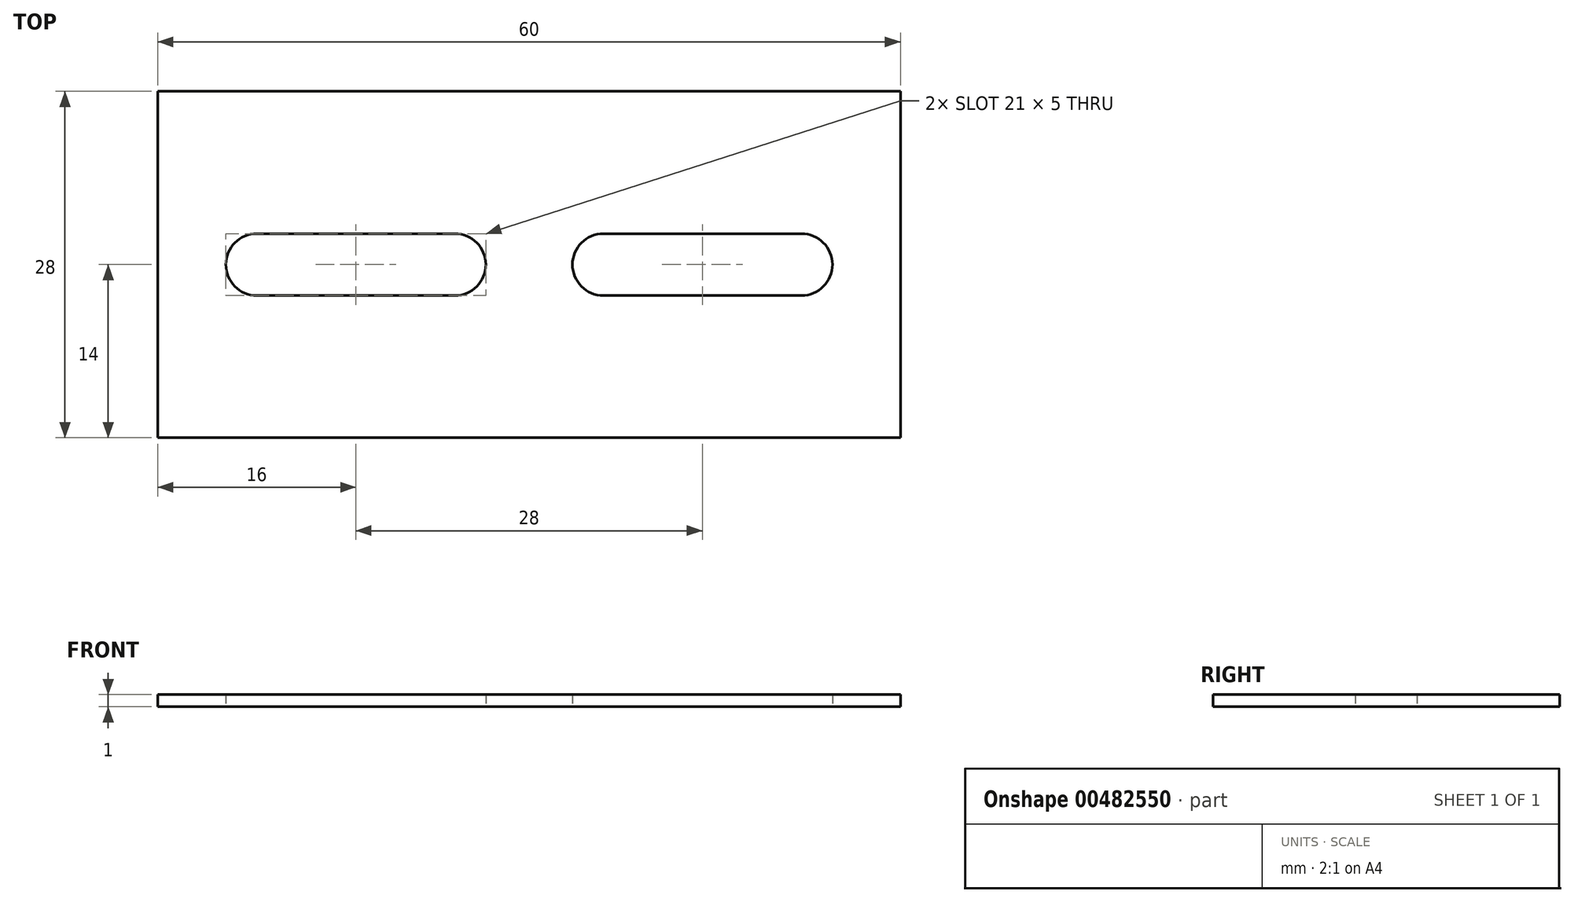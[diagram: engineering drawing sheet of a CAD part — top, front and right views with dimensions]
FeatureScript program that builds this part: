
annotation { "Feature Type Name" : "Feature", "Feature Type Description" : "" }
export const myFeature = defineFeature(function(context is Context, id is Id, definition is map)
    precondition{}
    {
        {
            var Q0;
            Q0=qCreatedBy(makeId("Top.planeOp"),FACE);
            var sketch = newSketch(context, id + "F0", { "sketchPlane" : qUnion([Q0])});
            skLineSegment(sketch, "E0.bottom", {"start": v(30, 14) * mm, "end": v(-30, 14) * mm});
            skLineSegment(sketch, "E0.top", {"start": v(30, -14) * mm, "end": v(-30, -14) * mm});
            skLineSegment(sketch, "E0.left", {"start": v(30, 14) * mm, "end": v(30, -14) * mm});
            skLineSegment(sketch, "E0.right", {"start": v(-30, 14) * mm, "end": v(-30, -14) * mm});
            skPoint(sketch, "E0.middle", {"position": v(0, 0) * mm});
            skLineSegment(sketch, "E1.bottom", {"start": v(-6, -2.5) * mm, "end": v(-22, -2.5) * mm});
            skLineSegment(sketch, "E1.top", {"start": v(-6, 2.5) * mm, "end": v(-22, 2.5) * mm});
            skPoint(sketch, "E1.middle", {"position": v(-14, 0) * mm});
            skArc(sketch, "E2", {"start": v(-22, 2.5) * mm, "mid": v(-24.5, 0) * mm, "end": v(-22, -2.5) * mm});
            skArc(sketch, "E3", {"start": v(-6, 2.5) * mm, "mid": v(-3.5, 0) * mm, "end": v(-6, -2.5) * mm});
            skLineSegment(sketch, "E4", {"start": v(0, 14) * mm, "end": v(0, -14) * mm, "construction": true});
            skPoint(sketch, "E5.MirrorP", {"position": v(14, 0) * mm});
            skArc(sketch, "E6.MirrorCS", {"start": v(6, 2.5) * mm, "mid": v(3.5, 0) * mm, "end": v(6, -2.5) * mm});
            skArc(sketch, "E7.MirrorCS", {"start": v(22, 2.5) * mm, "mid": v(24.5, 0) * mm, "end": v(22, -2.5) * mm});
            skLineSegment(sketch, "E8.MirrorCS", {"start": v(6, 2.5) * mm, "end": v(22, 2.5) * mm});
            skLineSegment(sketch, "E9.MirrorCS", {"start": v(6, -2.5) * mm, "end": v(22, -2.5) * mm});
            skSolve(sketch);
        }
        {
            var Q0;
            Q0=makeQuery(id+"F0.imprint","IMPRINT",FACE,{"disambiguationData":[TD([[makeQuery(id+"F0.imprint","IMPRINT",EDGE,{"derivedFrom":sQuery(id+"F0.wireOp",EDGE,"E0.bottom")}),1.0]])]});
            extrude(context, id + "F1", {"entities" : qUnion([Q0]), "depth" : 1 * mm});
        }
    });
